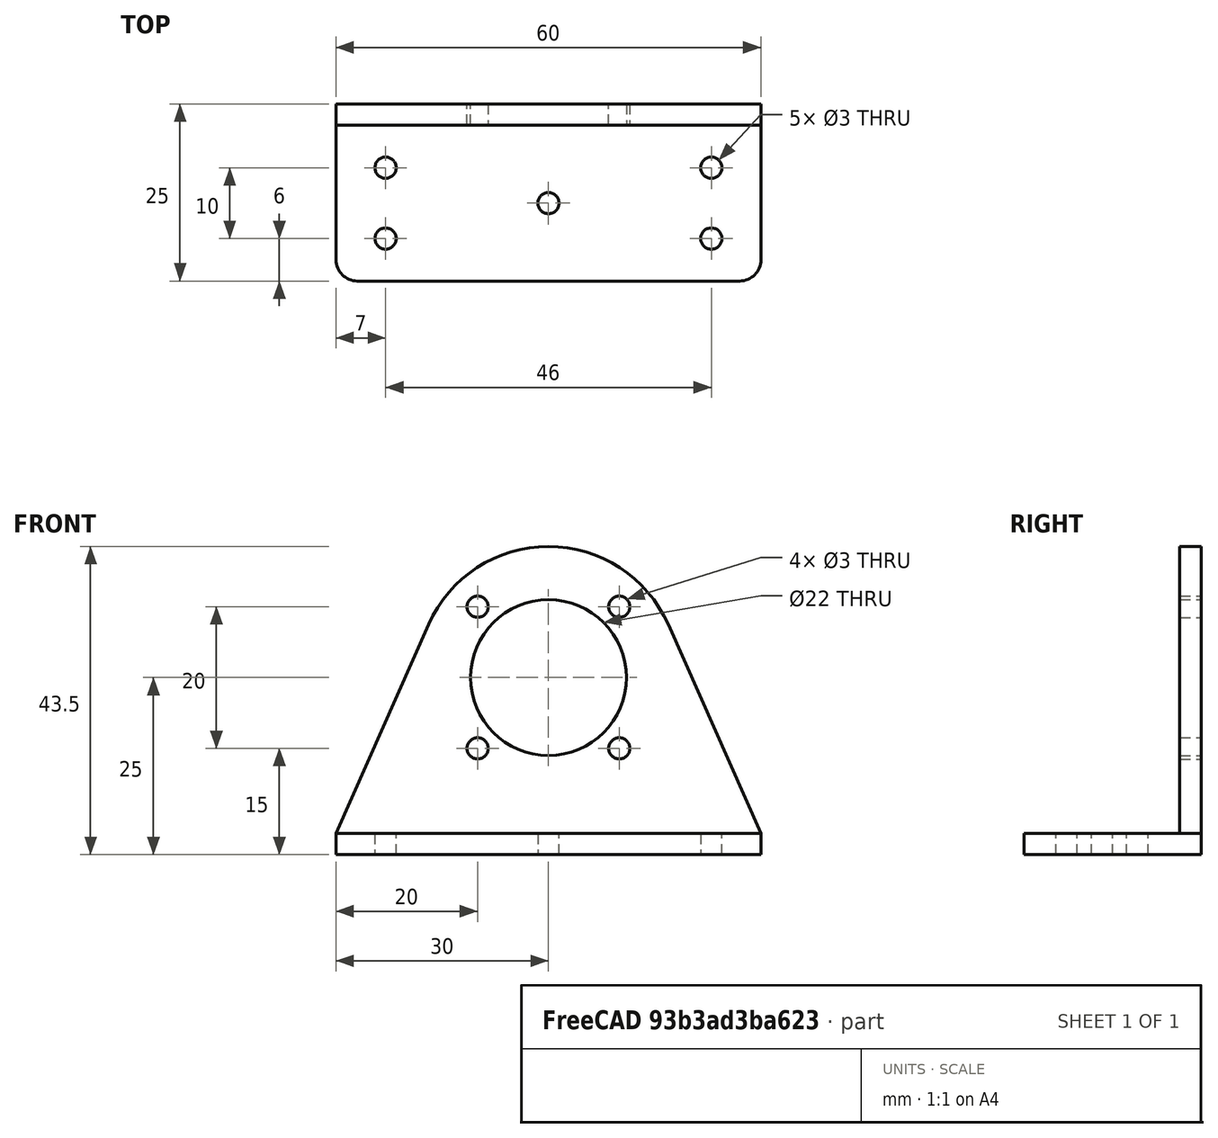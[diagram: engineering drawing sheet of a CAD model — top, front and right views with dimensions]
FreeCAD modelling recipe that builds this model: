
FCSTD DOCUMENT  (FreeCAD 1.0R39319 (Git))
Label: Motor-PG36Holder
License: All rights reserved
LicenseURL: http://en.wikipedia.org/wiki/All_rights_reserved
objects: TechDraw::DrawViewDimension×7, TechDraw::DrawProjGroupItem×5, Sketcher::SketchObject×3, PartDesign::Pad×2, PartDesign::Pocket×1, PartDesign::Fillet×1, PartDesign::Body×1, TechDraw::DrawSVGTemplate×1, TechDraw::DrawProjGroup×1, TechDraw::DrawViewImage×1, TechDraw::DrawPage×1
note: 19 computed .brp shape members not serialized (recipe doc carries the construction recipe); baked Part::Feature solids carry a one-line shape summary decoded from their .brp

FEATURE [Sketcher::SketchObject] Sketch
  ArcFitTolerance = 0
  AttachmentSupport = -> [XZ_Plane]
  FullyConstrained = true
  MakeInternals = false
  MapMode = 5
  Placement = pos=(0,0,0) rot=(1,0,0;1.5708rad)
  sketch-geometry (11):
    g0: ArcOfCircle CenterX=0 CenterY=25 CenterZ=0 NormalX=0 NormalY=0 NormalZ=1 AngleXU=0 Radius=18.5 StartAngle=0.417583 EndAngle=2.72401
    g1: LineSegment StartX=-30 StartY=0 StartZ=0 EndX=30 EndY=0 EndZ=0
    g2: LineSegment StartX=-30 StartY=0 StartZ=0 EndX=-30 EndY=3 EndZ=0
    g3: LineSegment StartX=-30 StartY=3 StartZ=0 EndX=-16.9103 EndY=32.5027 EndZ=0
    g4: LineSegment StartX=30 StartY=0 StartZ=0 EndX=30 EndY=3 EndZ=0
    g5: LineSegment StartX=30 StartY=3 StartZ=0 EndX=16.9103 EndY=32.5027 EndZ=0
    g6: Circle CenterX=10 CenterY=15 CenterZ=0 NormalX=0 NormalY=0 NormalZ=1 AngleXU=0 Radius=1.5
    g7: Circle CenterX=10 CenterY=35 CenterZ=0 NormalX=0 NormalY=0 NormalZ=1 AngleXU=0 Radius=1.5
    g8: Circle CenterX=-10 CenterY=35 CenterZ=0 NormalX=0 NormalY=0 NormalZ=1 AngleXU=0 Radius=1.5
    g9: Circle CenterX=-10 CenterY=15 CenterZ=0 NormalX=0 NormalY=0 NormalZ=1 AngleXU=0 Radius=1.5
    g10: Circle CenterX=0 CenterY=25 CenterZ=0 NormalX=0 NormalY=0 NormalZ=1 AngleXU=0 Radius=11
  constraints (31):
    c: PointOnObject(g0,g-2)
    c: Radius(g0) = 18.5
    c: PointOnObject(g1,g-1)
    c: Horizontal(g0,g0)
    c: Symmetric(g1,g1,g-2)
    c: Coincident(g1,g2)
    c: Vertical(g2)
    c: Coincident(g2,g3)
    c: Coincident(g1,g4)
    c: Coincident(g4,g5)
    c: Coincident(g5,g0)
    c: DistanceX(g1,g1) = 60
    c: Vertical(g4)
    c: Equal(g2,g4)
    c: DistanceY(g4,g4) = 3
    c: DistanceY(g-1,g0) = 25
    c: Tangent(g0,g3) = 1.5708
    c: Equal(g6,g7)
    c: Equal(g7,g8)
    c: Equal(g8,g9)
    c: Diameter(g6) = 3
    c: DistanceX(g6) = 10
    c: DistanceY(g6) = 15
    c: DistanceY(g6,g7) = 20
    c: DistanceX(g8,g7) = 20
    c: Vertical(g9,g8)
    c: Horizontal(g9,g6)
    c: Vertical(g7,g6)
    c: Horizontal(g8,g7)
    c: Coincident(g10,g0)
    c: Diameter(g10) = 22
FEATURE [PartDesign::Pad] Pad
  AllowMultiFace = false
  Direction = (0,-1,2e-16)
  Length = 3
  Length2 = 100
  Placement = pos=(0,0,0) rot=(1,0,0;1.5708rad)
  Profile = -> Sketch
  Suppressed = false
  Type = 0
FEATURE [Sketcher::SketchObject] Sketch002
  ArcFitTolerance = 0
  FullyConstrained = true
  MakeInternals = false
  MapMode = 5
  Placement = pos=(0,3e-15,3) rot=(0,0,1;3.14159rad)
  sketch-geometry (5):
    g0: Circle CenterX=23 CenterY=19 CenterZ=0 NormalX=0 NormalY=0 NormalZ=1 AngleXU=0 Radius=1.5
    g1: Circle CenterX=23 CenterY=9 CenterZ=0 NormalX=0 NormalY=0 NormalZ=1 AngleXU=0 Radius=1.5
    g2: Circle CenterX=-23 CenterY=19 CenterZ=0 NormalX=0 NormalY=0 NormalZ=1 AngleXU=0 Radius=1.5
    g3: Circle CenterX=-23 CenterY=9 CenterZ=0 NormalX=0 NormalY=0 NormalZ=1 AngleXU=0 Radius=1.5
    g4: Circle CenterX=0 CenterY=14 CenterZ=0 NormalX=0 NormalY=0 NormalZ=1 AngleXU=0 Radius=1.5
  constraints (14):
    c: Equal(g1,g0)
    c: Equal(g0,g2)
    c: Equal(g2,g3)
    c: Diameter(g1) = 3
    c: Symmetric(g1,g3,g-2)
    c: DistanceY(g1,g0) = 10
    c: Vertical(g0,g1)
    c: Horizontal(g0,g2)
    c: Vertical(g2,g3)
    c: DistanceX(g2,g0) = 46
    c: DistanceY(g-1,g1) = 9
    c: PointOnObject(g4,g-2)
    c: Equal(g4,g0)
    c: DistanceY(g-1,g4) = 14
FEATURE [Sketcher::SketchObject] Sketch003  label="Sketch001"
  ArcFitTolerance = 0
  AttachmentSupport = -> [Pad]
  FullyConstrained = true
  MakeInternals = false
  MapMode = 5
  Placement = pos=(0,-3,0) rot=(1,0,0;1.5708rad)
  sketch-geometry (4):
    g0: LineSegment StartX=-30 StartY=0 StartZ=0 EndX=30 EndY=0 EndZ=0
    g1: LineSegment StartX=30 StartY=0 StartZ=0 EndX=30 EndY=3 EndZ=0
    g2: LineSegment StartX=30 StartY=3 StartZ=0 EndX=-30 EndY=3 EndZ=0
    g3: LineSegment StartX=-30 StartY=3 StartZ=0 EndX=-30 EndY=0 EndZ=0
  constraints (11):
    c: Coincident(g0,g1)
    c: Coincident(g1,g2)
    c: Coincident(g2,g3)
    c: Coincident(g3,g0)
    c: Horizontal(g2)
    c: Vertical(g1)
    c: Vertical(g3)
    c: PointOnObject(g0,g-1)
    c: DistanceY(g1,g1) = 3
    c: Symmetric(g0,g0,g-2)
    c: DistanceX(g0,g0) = 60
FEATURE [PartDesign::Pad] Pad001
  AllowMultiFace = false
  BaseFeature = -> Pad
  Direction = (0,-1,2e-16)
  Length = 22
  Length2 = 100
  Placement = pos=(0,0,0) rot=(1,0,0;1.5708rad)
  Profile = -> Sketch003
  Suppressed = false
  Type = 0
FEATURE [PartDesign::Pocket] Pocket
  AllowMultiFace = false
  BaseFeature = -> Pad001
  Direction = (0,-1e-15,-1)
  Length = 3
  Length2 = 100
  Placement = pos=(0,0,0) rot=(1,0,0;1.5708rad)
  Profile = -> Sketch002
  Suppressed = false
  Type = 0
FEATURE [PartDesign::Fillet] Fillet
  Base = -> Pocket [Edge34,Edge30]
  BaseFeature = -> Pocket
  Placement = pos=(0,0,0) rot=(1,0,0;1.5708rad)
  Radius = 3
  Refine = true
  SupportTransform = false
  Suppressed = false
  UseAllEdges = false
FEATURE [PartDesign::Body] Body
  AllowCompound = false
  Group = -> [Sketch,Pad,Sketch003,Pad001,Sketch002,Pocket,Fillet]
  Origin = -> Origin
  Tip = -> Fillet
FEATURE [TechDraw::DrawSVGTemplate] Template
  EditableTexts = AUTHOR_NAME=Suharyono; DATE=2019-12-07; DN=DN; OWNER_NAME=Wizurai CP; PM=Aluminium; PN=PN; REVISION=REV A; RIGHTS=(R) DO NOT DUPLICATE THIS DRAWING TO THIRD PARTIES WITHOUT OWNER'S PERMISSION !; SCALE=M 1:1.5; SHEET=99 of 99; SIZE=A4; TITLELINE-1=AGV Mobile Robot V1.0
  Height = 210
  Orientation = 1
  Width = 297
FEATURE [TechDraw::DrawProjGroupItem] ProjItem  label="Front"
  CoarseView = false
  Direction = (0,1,0)
  Focus = 100
  HardHidden = false
  IsoCount = 0
  IsoHidden = false
  IsoVisible = false
  LockPosition = true
  Perspective = false
  Rotation = 0
  RotationVector = (-1,0,0)
  ScaleType = 2
  ScrubCount = 1
  SeamHidden = false
  SeamVisible = false
  SmoothHidden = false
  SmoothVisible = false
  Source = -> [Fillet]
  Type = 0
  X = 0
  XDirection = (-1,0,0)
  Y = 0
FEATURE [TechDraw::DrawProjGroupItem] ProjItem001  label="Left"
  CoarseView = true
  Direction = (1,1e-16,0)
  Focus = 100
  HardHidden = false
  IsoCount = 0
  IsoHidden = false
  IsoVisible = false
  LockPosition = false
  Perspective = false
  Rotation = 0
  RotationVector = (-1e-16,1,0)
  ScaleType = 2
  ScrubCount = 1
  SeamHidden = false
  SeamVisible = false
  SmoothHidden = false
  SmoothVisible = false
  Source = -> [Fillet]
  Type = 1
  X = 74.4307
  XDirection = (-1e-16,1,0)
  Y = 0
FEATURE [TechDraw::DrawProjGroupItem] ProjItem002  label="Isometric"
  CoarseView = true
  Direction = (1,1,-1)
  Focus = 100
  HardHidden = true
  IsoCount = 0
  IsoHidden = false
  IsoVisible = false
  LockPosition = true
  Perspective = false
  Rotation = 0
  RotationVector = (-1,1,0)
  ScaleType = 2
  ScrubCount = 1
  SeamHidden = false
  SeamVisible = false
  SmoothHidden = true
  SmoothVisible = false
  Source = -> [Fillet]
  Type = 8
  X = 151.141
  XDirection = (-1,1,0)
  Y = 51.5096
FEATURE [TechDraw::DrawProjGroupItem] ProjItem003  label="Top"
  CoarseView = true
  Direction = (0,0,-1)
  Focus = 100
  HardHidden = false
  IsoCount = 0
  IsoHidden = false
  IsoVisible = false
  LockPosition = true
  Perspective = false
  Rotation = 0
  RotationVector = (-1,0,0)
  ScaleType = 2
  ScrubCount = 1
  SeamHidden = false
  SeamVisible = false
  SmoothHidden = false
  SmoothVisible = false
  Source = -> [Fillet]
  Type = 5
  X = 0
  XDirection = (-1,0,0)
  Y = 59.6098
FEATURE [TechDraw::DrawProjGroupItem] ProjItem004  label="Bottom."
  CoarseView = true
  Direction = (0,0,1)
  Focus = 100
  HardHidden = false
  IsoCount = 0
  IsoHidden = false
  IsoVisible = false
  LockPosition = true
  Perspective = false
  Rotation = 0
  RotationVector = (-1,0,0)
  ScaleType = 2
  ScrubCount = 1
  SeamHidden = false
  SeamVisible = false
  SmoothHidden = false
  SmoothVisible = false
  Source = -> [Fillet]
  Type = 4
  X = 0
  XDirection = (-1,0,0)
  Y = -63.0118
FEATURE [TechDraw::DrawProjGroup] ProjGroup
  Anchor = -> ProjItem
  AutoDistribute = true
  LockPosition = false
  ProjectionType = 0
  Rotation = 0
  ScaleType = 0
  Source = -> [Fillet]
  Views = -> [ProjItem,ProjItem001,ProjItem002,ProjItem003,ProjItem004]
  X = 73.7462
  Y = 105.375
  spacingX = 15
  spacingY = 15
FEATURE [TechDraw::DrawViewDimension] Dimension003
  AngleOverride = false
  Arbitrary = false
  ArbitraryTolerances = false
  EqualTolerance = false
  ExtensionAngle = 0
  FormatSpec = ⌀%.2f
  FormatSpecOverTolerance = %+.2w
  FormatSpecUnderTolerance = %+.2w
  Inverted = false
  LineAngle = 0
  LockPosition = false
  MeasureType = 1
  OverTolerance = 0
  References2D = -> [ProjItem]
  Rotation = 0
  ScaleType = 0
  TheoreticalExact = false
  Type = 5
  UnderTolerance = 0
  X = -23.3368
  Y = 29.2545
FEATURE [TechDraw::DrawViewDimension] Dimension004
  AngleOverride = false
  Arbitrary = false
  ArbitraryTolerances = false
  EqualTolerance = false
  ExtensionAngle = 0
  FormatSpec = ⌀%.2f
  FormatSpecOverTolerance = %+.2w
  FormatSpecUnderTolerance = %+.2w
  Inverted = false
  LineAngle = 0
  LockPosition = false
  MeasureType = 1
  OverTolerance = 0
  References2D = -> [ProjItem]
  Rotation = 0
  ScaleType = 0
  TheoreticalExact = false
  Type = 5
  UnderTolerance = 0
  X = 35.3343
  Y = 27.0385
FEATURE [TechDraw::DrawViewDimension] Dimension005
  AngleOverride = false
  Arbitrary = false
  ArbitraryTolerances = false
  EqualTolerance = false
  ExtensionAngle = 0
  FormatSpec = ⌀%.2f
  FormatSpecOverTolerance = %+.2w
  FormatSpecUnderTolerance = %+.2w
  Inverted = false
  LineAngle = 0
  LockPosition = false
  MeasureType = 1
  OverTolerance = 0
  References2D = -> [ProjItem]
  Rotation = 0
  ScaleType = 0
  TheoreticalExact = false
  Type = 5
  UnderTolerance = 0
  X = -40.8002
  Y = 15.6389
FEATURE [TechDraw::DrawViewDimension] Dimension006
  AngleOverride = false
  Arbitrary = false
  ArbitraryTolerances = false
  EqualTolerance = false
  ExtensionAngle = 0
  FormatSpec = %.2f
  FormatSpecOverTolerance = %+.2w
  FormatSpecUnderTolerance = %+.2w
  Inverted = false
  LineAngle = 0
  LockPosition = false
  MeasureType = 1
  OverTolerance = 0
  References2D = -> [ProjItem001]
  Rotation = 0
  ScaleType = 0
  TheoreticalExact = false
  Type = 2
  UnderTolerance = 0
  X = 22.3127
  Y = 3.12505
FEATURE [TechDraw::DrawViewDimension] Dimension007
  AngleOverride = false
  Arbitrary = false
  ArbitraryTolerances = false
  EqualTolerance = false
  ExtensionAngle = 0
  FormatSpec = %.2f
  FormatSpecOverTolerance = %+.2w
  FormatSpecUnderTolerance = %+.2w
  Inverted = false
  LineAngle = 0
  LockPosition = false
  MeasureType = 1
  OverTolerance = 0
  References2D = -> [ProjItem001]
  Rotation = 0
  ScaleType = 0
  TheoreticalExact = false
  Type = 1
  UnderTolerance = 0
  X = 1.09377
  Y = -37.344
FEATURE [TechDraw::DrawViewDimension] Dimension
  AngleOverride = false
  Arbitrary = false
  ArbitraryTolerances = false
  EqualTolerance = false
  ExtensionAngle = 0
  FormatSpec = ⌀%.2f
  FormatSpecOverTolerance = %+.2w
  FormatSpecUnderTolerance = %+.2w
  Inverted = false
  LineAngle = 0
  LockPosition = false
  MeasureType = 1
  OverTolerance = 0
  References2D = -> [ProjItem003]
  Rotation = 0
  ScaleType = 0
  TheoreticalExact = false
  Type = 5
  UnderTolerance = 0
  X = 46.3912
  Y = -5.3108
FEATURE [TechDraw::DrawViewDimension] Dimension008
  AngleOverride = false
  Arbitrary = false
  ArbitraryTolerances = false
  EqualTolerance = false
  ExtensionAngle = 0
  FormatSpec = %.2f
  FormatSpecOverTolerance = %+.2w
  FormatSpecUnderTolerance = %+.2w
  Inverted = false
  LineAngle = 0
  LockPosition = false
  MeasureType = 1
  OverTolerance = 0
  References2D = -> [ProjItem]
  Rotation = 0
  ScaleType = 0
  TheoreticalExact = false
  Type = 1
  UnderTolerance = 0
  X = 3.51415
  Y = -37.3714
FEATURE [TechDraw::DrawViewImage] Image
  Height = 600
  ImageFile = <path> - AGV robot/FreeCad - AGV Process/Assy AGV PG36 Omni/Motor-PG36Holder.png
  LockPosition = true
  Rotation = 0
  Scale = 1.5
  ScaleType = 2
  Width = 700
  X = 225.134
  Y = 85.6415
FEATURE [TechDraw::DrawPage] Page
  KeepUpdated = true
  NextBalloonIndex = 1
  ProjectionType = 0
  Template = -> Template
  Views = -> [ProjGroup,Dimension003,Dimension004,Dimension005,Dimension006,Dimension007,Dimension,Dimension008,Image]
note: 1 file-system path scrubbed to <path> (originals preserved in the JSON sidecar)
